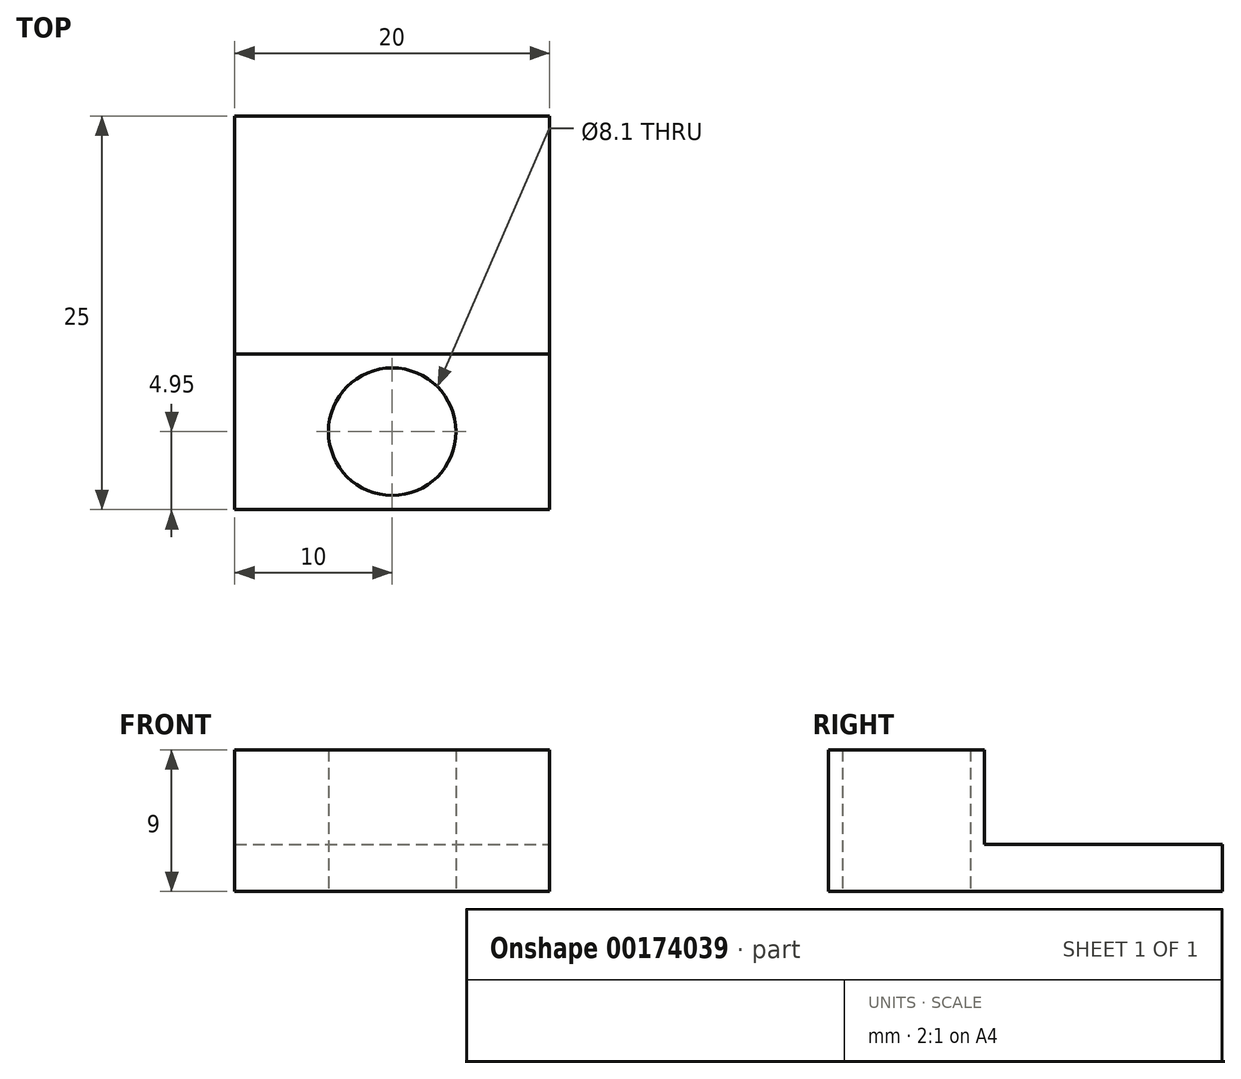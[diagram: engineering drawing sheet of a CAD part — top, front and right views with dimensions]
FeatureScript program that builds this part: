
annotation { "Feature Type Name" : "Feature", "Feature Type Description" : "" }
export const myFeature = defineFeature(function(context is Context, id is Id, definition is map)
    precondition{}
    {
        {
            var Q0;
            Q0=qCreatedBy(makeId("Top.planeOp"),FACE);
            var sketch = newSketch(context, id + "F0", { "sketchPlane" : qUnion([Q0])});
            skLineSegment(sketch, "E0.bottom", {"start": v(-10, 12.5) * mm, "end": v(10, 12.5) * mm});
            skLineSegment(sketch, "E0.top", {"start": v(-10, -12.5) * mm, "end": v(10, -12.5) * mm});
            skLineSegment(sketch, "E0.left", {"start": v(-10, 12.5) * mm, "end": v(-10, -12.5) * mm});
            skLineSegment(sketch, "E0.right", {"start": v(10, 12.5) * mm, "end": v(10, -12.5) * mm});
            skPoint(sketch, "E1", {"position": v(0, 12.5) * mm});
            skPoint(sketch, "E2", {"position": v(-10, 0) * mm});
            skSolve(sketch);
        }
        {
            var Q0;
            Q0 = qSketchRegion(id + "F0", true);
            extrude(context, id + "F1", {"entities" : qUnion([Q0]), "depth" : 3 * mm});
        }
        {
            var Q0;
            Q0=qCreatedBy(makeId("Top.planeOp"),FACE);
            var sketch = newSketch(context, id + "F2", { "sketchPlane" : qUnion([Q0])});
            skLineSegment(sketch, "E3.0", {"start": v(-10, -2.6) * mm, "end": v(10, -2.6) * mm});
            skLineSegment(sketch, "E4.0", {"start": v(-10, -2.6) * mm, "end": v(-10, -12.5) * mm});
            skLineSegment(sketch, "E5.0", {"start": v(10, -2.6) * mm, "end": v(10, -12.5) * mm});
            skPoint(sketch, "E6.orphan", {"position": v(-10, 12.5) * mm});
            skPoint(sketch, "E7.orphan", {"position": v(10, 12.5) * mm});
            skCircle(sketch, "E8", {"center": v(0, -7.55) * mm, "radius": 4.05 * mm, "construction": true});
            skLineSegment(sketch, "E9", {"start": v(10, -2.6) * mm, "end": v(10, -7.5) * mm});
            skLineSegment(sketch, "E10", {"start": v(-10, -2.6) * mm, "end": v(-10, -6.8) * mm});
            skLineSegment(sketch, "E11.0", {"start": v(-10, -12.5) * mm, "end": v(10, -12.5) * mm});
            skSolve(sketch);
        }
        {
            var Q0;
            Q0 = qSketchRegion(id + "F2", true);
            var Q1;
            Q1 = qConstructionFilter(qBodyType(qCreatedBy(id + "F2" ,EDGE), BodyType.WIRE), ConstructionObject.NO);
            extrude(context, id + "F3", {"entities" : qUnion([Q0]), "operationType" : NewBodyOperationType.ADD, "surfaceEntities" : qUnion([Q1]), "depth" : 9 * mm});
        }
        {
            var Q0;
            Q0=qCreatedBy(makeId("Top.planeOp"),FACE);
            var sketch = newSketch(context, id + "F4", { "sketchPlane" : qUnion([Q0])});
            skCircle(sketch, "E12.0", {"center": v(0, -7.55) * mm, "radius": 4.05 * mm});
            skSolve(sketch);
        }
        {
            var Q0;
            Q0 = qSketchRegion(id + "F4", true);
            var Q1;
            Q1 = qConstructionFilter(qBodyType(qCreatedBy(id + "F4" ,EDGE), BodyType.WIRE), ConstructionObject.NO);
            var Q2;
            Q2=makeQuery(id+"F3.opExtrude","CAP_FACE",FACE,{"disambiguationData":[OSD([sQuery(id+"F2.wireOp",EDGE,"E3.0"),sQuery(id+"F2.wireOp",EDGE,"a2q0104G-Bl7I-Rjex-EUNp-YHxzSH3oDlM2"),sQuery(id+"F2.wireOp",EDGE,"E9"),sQuery(id+"F2.wireOp",EDGE,"E10")])],"isStart":false});
            var Q3;
            Q3=makeQuery(id+"F1.opExtrude","SWEPT_BODY",BODY,{"disambiguationData":[OSD([sQuery(id+"F0.wireOp",EDGE,"E0.bottom"),sQuery(id+"F0.wireOp",EDGE,"E0.top"),sQuery(id+"F0.wireOp",EDGE,"E0.left"),sQuery(id+"F0.wireOp",EDGE,"E0.right")])]});
            extrude(context, id + "F5", {"entities" : qUnion([Q0]), "operationType" : NewBodyOperationType.REMOVE, "surfaceEntities" : qUnion([Q1]), "endBound" : BoundingType.UP_TO_SURFACE, "endBoundEntityFace" : qUnion([Q2]), "endBoundEntityBody" : qUnion([Q3]), "depth" : 25 * mm});
        }
    });
